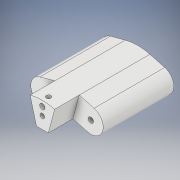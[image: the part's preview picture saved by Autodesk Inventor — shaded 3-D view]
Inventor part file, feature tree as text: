
AUTODESK INVENTOR PART (.ipt)
format: ipt  version: 2017 SP1 (Build 210196100, 196)  size: 168,960 bytes
history: native  units: in
note: dims shown in document units (in); Inventor stores cm internally (conversion verified against a paired STEP export)
features: extrude x6, sketch x6
ambient origin geometry x8: Origin, YZ Plane, XZ Plane, XY Plane, X Axis, Y Axis, Z Axis, Center Point
bodies: Solid1 (feature_tree)
feature tree (12):
  extrude  "Extrusion1"  Depth=0.3937in TaperAngle=0.0deg
  extrude  "Extrusion2"  Depth=0.1378in
  extrude  "Extrusion3"  Depth=0.5118in
  extrude  "Extrusion4"  Depth=0.6299in TaperAngle=0.0deg
  extrude  "Extrusion5"  Depth=0.6299in TaperAngle=0.0deg
  extrude  "Extrusion6"  Depth=0.1575in
  sketch  "Sketch1"  dims[d0=0.6299in d1=0.6299in d2=0.6299in d3=0.3937in d4=0.3937in d5=0.6299in d6=0.6299in d7=75.0deg d9=1.811in d10=0.0in]
  sketch  "Sketch2"  dims[d11=0.1378in d12=0.1378in]
  sketch  "Sketch3"  dims[d13=0.1378in d14=0.5118in]
  sketch  "Sketch4"  dims[d15=1.811in d16=0.0in d17=0.6299in d18=0.0in]
  sketch  "Sketch5"  dims[d19=0.1181in d20=0.6299in d21=0.0in]
  sketch  "Sketch6"  dims[d22=0.1181in d23=0.1575in d24=0.6299in d25=0.0in d26=0.1969in d27=0.0in]
